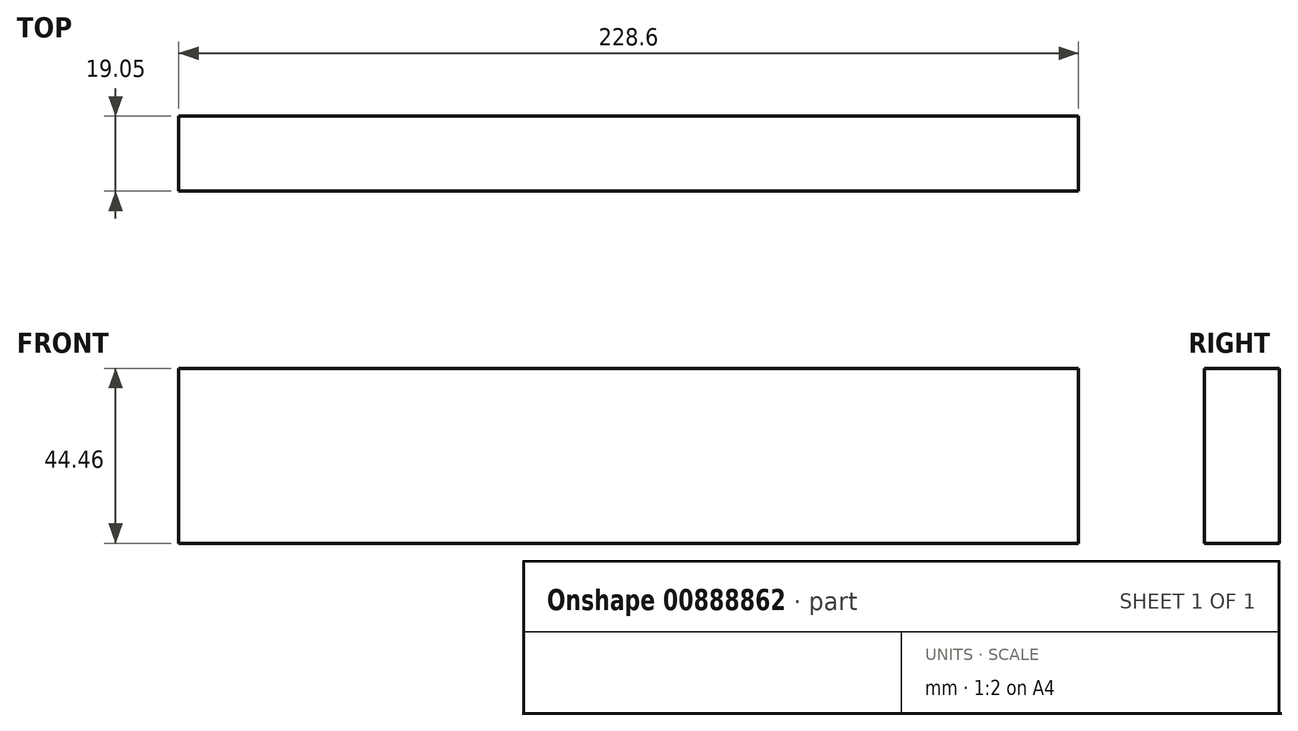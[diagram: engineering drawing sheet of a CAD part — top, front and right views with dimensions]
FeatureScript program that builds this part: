
annotation { "Feature Type Name" : "Feature", "Feature Type Description" : "" }
export const myFeature = defineFeature(function(context is Context, id is Id, definition is map)
    precondition{}
    {
        {
            var Q0;
            Q0=qCreatedBy(makeId("Front.planeOp"),FACE);
            var sketch = newSketch(context, id + "F0", { "sketchPlane" : qUnion([Q0])});
            skLineSegment(sketch, "E0.bottom", {"start": v(114.3, -22.22) * mm, "end": v(-114.3, -22.22) * mm});
            skLineSegment(sketch, "E0.top", {"start": v(114.3, 22.23) * mm, "end": v(-114.3, 22.23) * mm});
            skLineSegment(sketch, "E0.left", {"start": v(114.3, -22.22) * mm, "end": v(114.3, 22.23) * mm});
            skLineSegment(sketch, "E0.right", {"start": v(-114.3, -22.22) * mm, "end": v(-114.3, 22.23) * mm});
            skPoint(sketch, "E0.middle", {"position": v(0, 0) * mm});
            skSolve(sketch);
        }
        {
            var Q0;
            Q0=makeQuery(id+"F0.imprint","IMPRINT",FACE,{"disambiguationData":[TD([[makeQuery(id+"F0.imprint","IMPRINT",EDGE,{"derivedFrom":sQuery(id+"F0.wireOp",EDGE,"E0.bottom")}),-1.0]])]});
            extrude(context, id + "F1", {"entities" : qUnion([Q0]), "depth" : 19.05 * mm, "offsetDistance" : 25.4 * mm});
        }
    });
